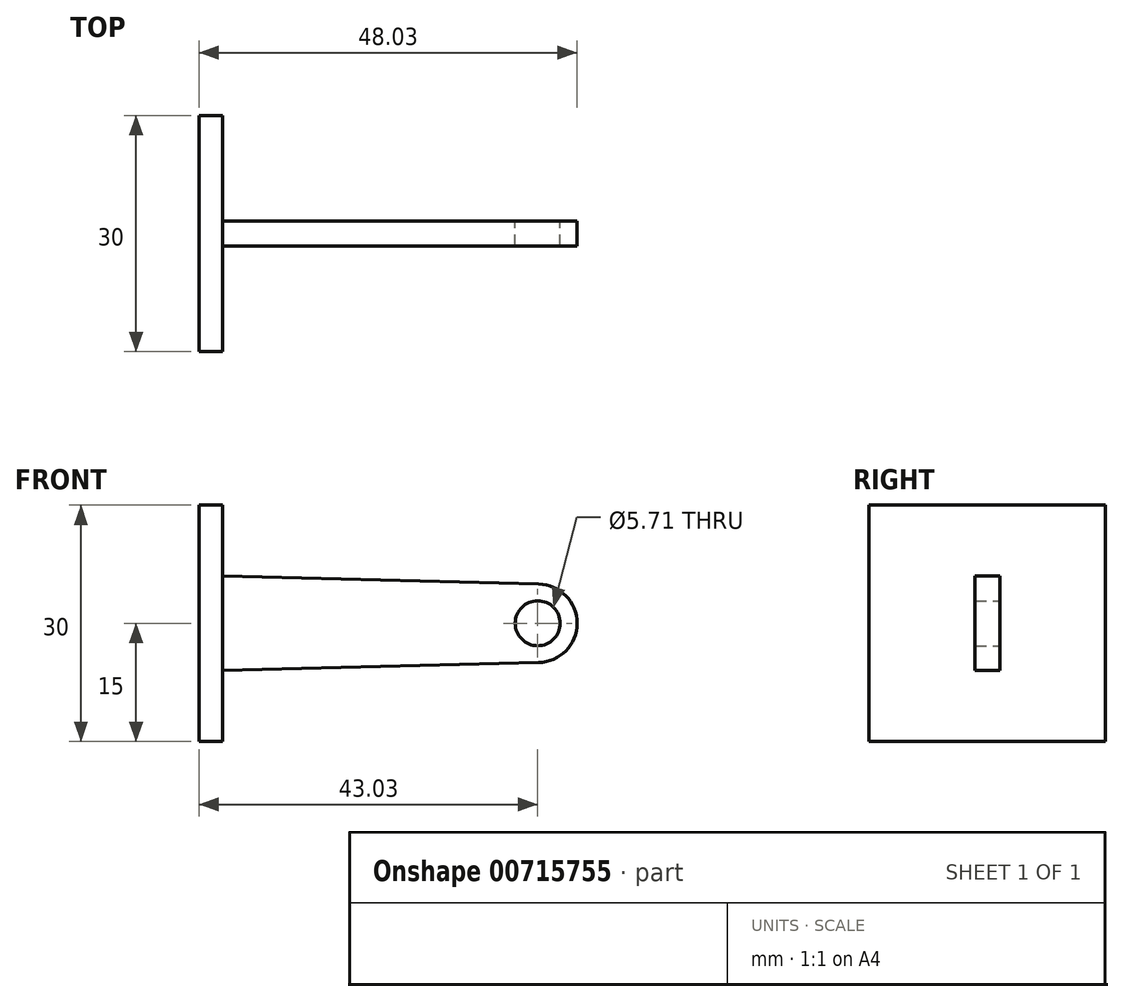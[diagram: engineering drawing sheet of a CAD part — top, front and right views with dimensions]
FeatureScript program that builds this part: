
annotation { "Feature Type Name" : "Feature", "Feature Type Description" : "" }
export const myFeature = defineFeature(function(context is Context, id is Id, definition is map)
    precondition{}
    {
        {
            var Q0;
            Q0=qCreatedBy(makeId("Front.planeOp"),FACE);
            var sketch = newSketch(context, id + "F0", { "sketchPlane" : qUnion([Q0])});
            skCircle(sketch, "E0", {"center": v(0, 0) * mm, "radius": 2.85 * mm});
            skCircle(sketch, "E1", {"center": v(0, 0) * mm, "radius": 5 * mm, "construction": true});
            skLineSegment(sketch, "E2", {"start": v(-40, 6) * mm, "end": v(-40, -6) * mm});
            skLineSegment(sketch, "E3", {"start": v(-40, -6) * mm, "end": v(0.12, -5) * mm});
            skLineSegment(sketch, "E4", {"start": v(-40, 6) * mm, "end": v(0.12, 5) * mm});
            skArc(sketch, "E5", {"start": v(0.12, 5) * mm, "mid": v(5, 0) * mm, "end": v(0.12, -5) * mm});
            skSolve(sketch);
        }
        {
            var Q0;
            Q0=qSketchRegion(id+"F0",true);
            extrude(context, id + "F1", {"entities" : qUnion([Q0]), "depth" : 3.17 * mm, "offsetDistance" : 25 * mm, "symmetric" : true});
        }
        {
            var Q0;
            Q0=makeQuery(id+"F1.opExtrude","SWEPT_FACE",FACE,{"disambiguationData":[OSD([sQuery(id+"F0.wireOp",EDGE,"E2")])]});
            var sketch = newSketch(context, id + "F2", { "sketchPlane" : qUnion([Q0])});
            skLineSegment(sketch, "E6.bottom", {"start": v(-15, -15) * mm, "end": v(15, -15) * mm});
            skLineSegment(sketch, "E6.top", {"start": v(-15, 15) * mm, "end": v(15, 15) * mm});
            skLineSegment(sketch, "E6.left", {"start": v(-15, -15) * mm, "end": v(-15, 15) * mm});
            skLineSegment(sketch, "E6.right", {"start": v(15, -15) * mm, "end": v(15, 15) * mm});
            skSolve(sketch);
        }
        {
            var Q0;
            Q0=qSketchRegion(id+"F2",true);
            extrude(context, id + "F3", {"entities" : qUnion([Q0]), "operationType" : NewBodyOperationType.ADD, "depth" : (3.17 - 0.15) * mm, "offsetDistance" : 25 * mm});
        }
    });
